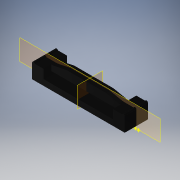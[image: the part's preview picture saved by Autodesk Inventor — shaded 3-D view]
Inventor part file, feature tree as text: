
AUTODESK INVENTOR PART (.ipt)
format: ipt  version: 2019 (Build 230136000, 136)  size: 227,840 bytes
history: native  units: mm (DEFAULTED — no unit token found)
features: other x16, sketch x8, extrude x5, fillet x1, pattern_linear x1
ambient origin geometry x8: Origin, YZ Plane, XZ Plane, XY Plane, X Axis, Y Axis, Z Axis, Center Point
bodies: Solid1 (feature_tree)
feature tree (31):
  extrude  "Extrusion1"  Depth=10.0mm
  extrude  "Extrusion2"  Depth=47.0mm
  extrude  "Extrusion3"  Depth=0.5842mm TaperAngle=0.0deg
  extrude  "Extrusion4"  Depth=2.54mm
  extrude  "Extrusion5"  Depth=1.3208mm
  fillet  "Fillet1"  Radius=0.762mm
  sketch  "Sketch8"  dims[d15=8.128mm]
  sketch  "Sketch9"  dims[d16=16.891mm]
  sketch  "Sketch11"  dims[d17=0.508mm d18=3.302mm d19=0.0mm d20=1.143mm d21=3.302mm d22=0.0mm d23=0.5842mm d37=0.508mm d38=0.5842mm d39=0.254mm d40=160.0mm d42=1.27mm d43=10.0mm d45=25.4mm d48=1.27mm d49=1.27mm d50=1.27mm d51=1.27mm d53=1.27mm d54=1.27mm d55=1.27mm d56=1.27mm d57=1.27mm d58=1.27mm d59=1.27mm d60=1.27mm d61=1.27mm d62=1.27mm d63=1.27mm d64=0.4318mm d65=2.032mm d66=20.0mm d68=22.86mm]
  pattern_linear  "Rectangular Pattern1"  Spacing1=3.302mm  [1 undecoded]
  sketch  "Sketch1"  dims[d0=40.0mm d1=10.0mm]
  sketch  "Sketch2"  dims[d2=7.4676mm d3=0.0mm d4=47.0mm]
  sketch  "Sketch3"  dims[d5=0.5842mm d6=7.4676mm d7=0.0mm]
  sketch  "Sketch4"  dims[d8=30.0mm d9=2.54mm]
  sketch  "Sketch5"  dims[d11=7.4676mm d12=0.0mm d13=1.3208mm d14=0.762mm]
  other  "Work Point66"
  other  "Work Point67"
  other  "Work Point68"
  other  "Work Point69"
  other  "Work Point70"
  other  "Work Point71"
  other  "Work Point72"
  other  "Work Point73"
  other  "Work Point74"
  other  "Work Point75"
  other  "Work Point76"
  other  "Work Point77"
  other  "Work Point78"
  other  "Work Point79"
  other  "Work Point80"
  other  "Work Point81"
note: 1 required parameter value undecoded (feature->parameter linkage not recoverable at this tier; creation-order binding heuristic only, values carry confidence <= 0.55)
